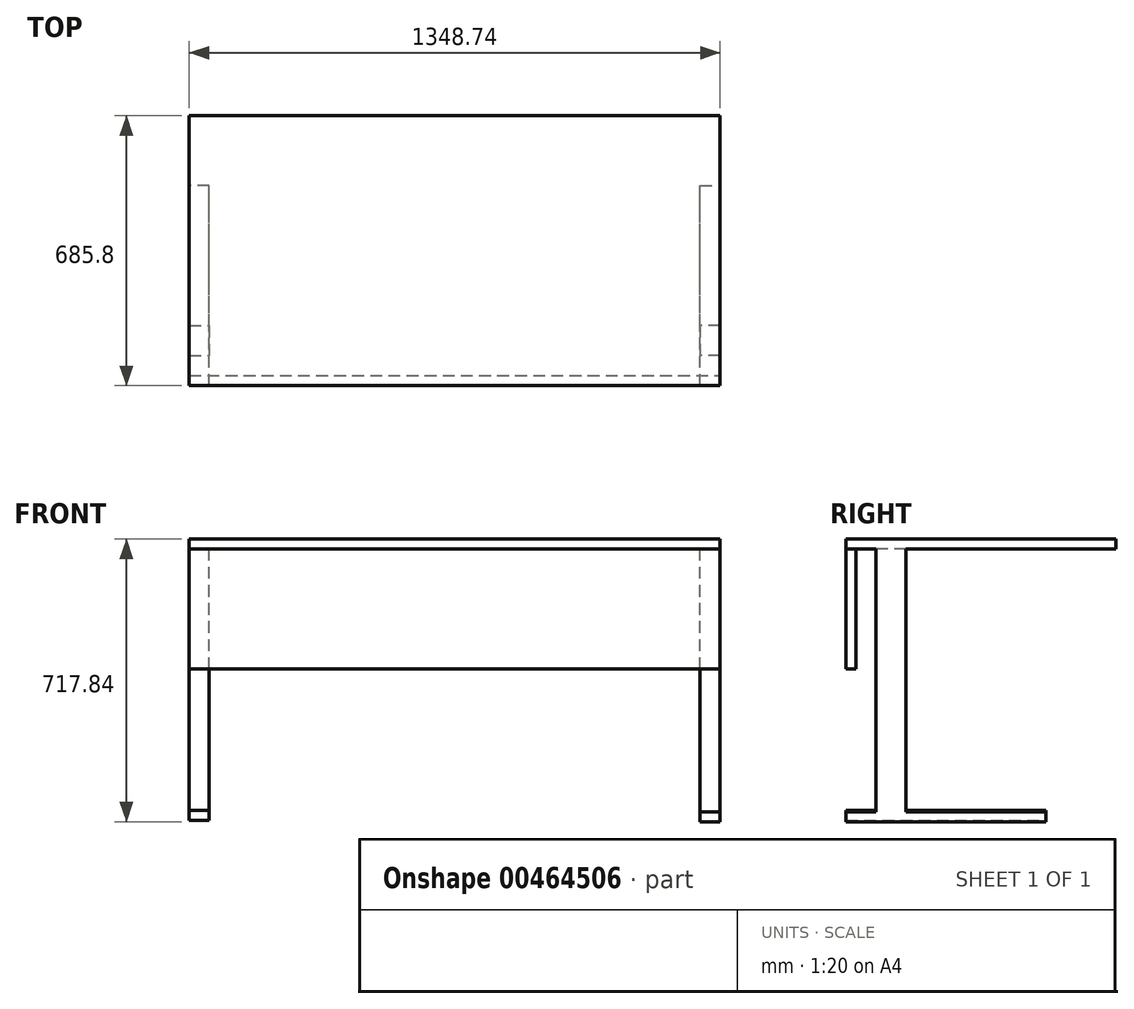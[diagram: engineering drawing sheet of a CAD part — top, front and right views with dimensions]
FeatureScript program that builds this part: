
annotation { "Feature Type Name" : "Feature", "Feature Type Description" : "" }
export const myFeature = defineFeature(function(context is Context, id is Id, definition is map)
    precondition{}
    {
        {
            var Q0;
            Q0=qCreatedBy(makeId("Top.planeOp"),FACE);
            var sketch = newSketch(context, id + "F0", { "sketchPlane" : qUnion([Q0])});
            skLineSegment(sketch, "E0.bottom", {"start": v(-75.15, -75.42) * mm, "end": v(1273.6, -75.42) * mm});
            skLineSegment(sketch, "E0.top", {"start": v(-75.15, 610.38) * mm, "end": v(1273.6, 610.38) * mm});
            skLineSegment(sketch, "E0.left", {"start": v(-75.15, -75.42) * mm, "end": v(-75.15, 610.38) * mm});
            skLineSegment(sketch, "E0.right", {"start": v(1273.6, -75.42) * mm, "end": v(1273.6, 610.38) * mm});
            skLineSegment(sketch, "E1.bottom", {"start": v(-75.15, 610.38) * mm, "end": v(5.86, 610.38) * mm});
            skLineSegment(sketch, "E1.left", {"start": v(-75.15, 610.38) * mm, "end": v(-75.15, 533.58) * mm});
            skSolve(sketch);
        }
        {
            var Q0;
            Q0 = qSketchRegion(id + "F0", true);
            extrude(context, id + "F1", {"entities" : qUnion([Q0]), "depth" : 25.4 * mm});
        }
        {
            var Q0;
            Q0=makeQuery(id+"F1.opExtrude","CAP_FACE",FACE,{"disambiguationData":[OSD([sQuery(id+"F0.wireOp",EDGE,"E0.bottom"),sQuery(id+"F0.wireOp",EDGE,"E0.top"),sQuery(id+"F0.wireOp",EDGE,"E0.left"),sQuery(id+"F0.wireOp",EDGE,"E0.right"),sQuery(id+"F0.wireOp",EDGE,"E1.bottom"),sQuery(id+"F0.wireOp",EDGE,"E1.left")])],"isStart":true});
            var sketch = newSketch(context, id + "F2", { "sketchPlane" : qUnion([Q0])});
            skLineSegment(sketch, "E2.bottom", {"start": v(-75.15, -76.98) * mm, "end": v(-24.35, -76.98) * mm});
            skLineSegment(sketch, "E2.top", {"start": v(-75.15, -0.78) * mm, "end": v(-24.35, -0.78) * mm});
            skLineSegment(sketch, "E2.left", {"start": v(-75.15, -76.98) * mm, "end": v(-75.15, -0.78) * mm});
            skLineSegment(sketch, "E2.right", {"start": v(-24.35, -76.98) * mm, "end": v(-24.35, -0.78) * mm});
            skLineSegment(sketch, "E3.bottom", {"start": v(1273.6, -76.98) * mm, "end": v(1222.8, -76.98) * mm});
            skLineSegment(sketch, "E3.top", {"start": v(1273.6, -0.78) * mm, "end": v(1222.8, -0.78) * mm});
            skLineSegment(sketch, "E3.left", {"start": v(1273.6, -76.98) * mm, "end": v(1273.6, -0.78) * mm});
            skLineSegment(sketch, "E3.right", {"start": v(1222.8, -76.98) * mm, "end": v(1222.8, -0.78) * mm});
            skSolve(sketch);
        }
        {
            var Q0;
            Q0=makeQuery(id+"F2.imprint","IMPRINT",FACE,{"disambiguationData":[TD([[makeQuery(id+"F2.imprint","IMPRINT",EDGE,{"derivedFrom":sQuery(id+"F2.wireOp",EDGE,"E2.bottom")}),1.0]])]});
            var Q1;
            Q1=makeQuery(id+"F2.imprint","IMPRINT",FACE,{"disambiguationData":[TD([[makeQuery(id+"F2.imprint","IMPRINT",EDGE,{"derivedFrom":sQuery(id+"F2.wireOp",EDGE,"E3.bottom")}),-1.0]])]});
            extrude(context, id + "F3", {"entities" : qUnion([Q0, Q1]), "operationType" : NewBodyOperationType.ADD, "depth" : 685.8 * mm});
        }
        {
            var Q0;
            Q0=makeQuery(id+"F3.boolean.opBoolean","MERGE",FACE,{"derivedFrom":[makeQuery(id+"F1.opExtrude","SWEPT_FACE",FACE,{"disambiguationData":[OSD([sQuery(id+"F0.wireOp",EDGE,"E0.right")])]}),makeQuery(id+"F3.opExtrude","SWEPT_FACE",FACE,{"disambiguationData":[OSD([sQuery(id+"F2.wireOp",EDGE,"E3.left")])]})]});
            var sketch = newSketch(context, id + "F4", { "sketchPlane" : qUnion([Q0])});
            skLineSegment(sketch, "E4.bottom", {"start": v(-75.42, -667.04) * mm, "end": v(432.58, -667.04) * mm});
            skLineSegment(sketch, "E4.top", {"start": v(-75.42, -692.44) * mm, "end": v(432.58, -692.44) * mm});
            skLineSegment(sketch, "E4.left", {"start": v(-75.42, -667.04) * mm, "end": v(-75.42, -692.44) * mm});
            skLineSegment(sketch, "E4.right", {"start": v(432.58, -667.04) * mm, "end": v(432.58, -692.44) * mm});
            skSolve(sketch);
        }
        {
            var Q0;
            Q0 = qSketchRegion(id + "FHoVi1I3KBmm1qh_1", true);
            var Q1;
            Q1=makeQuery(id+"F4.imprint","IMPRINT",FACE,{"disambiguationData":[TD([[makeQuery(id+"F4.imprint","IMPRINT",EDGE,{"derivedFrom":sQuery(id+"F4.wireOp",EDGE,"E4.top")}),1.0]])]});
            extrude(context, id + "F5", {"entities" : qUnion([Q0, Q1]), "operationType" : NewBodyOperationType.ADD, "oppositeDirection" : true, "depth" : 50.8 * mm});
        }
        {
            var Q0;
            Q0=makeQuery(id+"F3.boolean.opBoolean","MERGE",FACE,{"derivedFrom":[makeQuery(id+"F1.opExtrude","SWEPT_FACE",FACE,{"disambiguationData":[OSD([sQuery(id+"F0.wireOp",EDGE,"E0.left"),sQuery(id+"F0.wireOp",EDGE,"E1.left")])]}),makeQuery(id+"F3.opExtrude","SWEPT_FACE",FACE,{"disambiguationData":[OSD([sQuery(id+"F2.wireOp",EDGE,"E2.left")])]})]});
            var sketch = newSketch(context, id + "F6", { "sketchPlane" : qUnion([Q0])});
            skPoint(sketch, "E5.firstSnap0", {"position": v(-38.88, -685.8) * mm});
            skLineSegment(sketch, "E6.bottom", {"start": v(75.42, -664.12) * mm, "end": v(-432.58, -664.12) * mm});
            skLineSegment(sketch, "E6.top", {"start": v(75.42, -689.52) * mm, "end": v(-432.58, -689.52) * mm});
            skLineSegment(sketch, "E6.left", {"start": v(75.42, -664.12) * mm, "end": v(75.42, -689.52) * mm});
            skLineSegment(sketch, "E6.right", {"start": v(-432.58, -664.12) * mm, "end": v(-432.58, -689.52) * mm});
            skSolve(sketch);
        }
        {
            var Q0;
            {var subQ1=sQuery(id+"F2.wireOp",EDGE,"E2.left");var subQ8=makeQuery(id+"F3.opExtrude","CAP_EDGE",EDGE,{"disambiguationData":[OSD([subQ1])],"isStart":false});Q0=makeQuery(id+"F6.imprint","IMPRINT",FACE,{"disambiguationData":[TD([[makeQuery(id+"F6.imprint","IMPRINT",EDGE,{"derivedFrom":subQ8}),1.0]])]});}
            var Q1;
            Q1=makeQuery(id+"F6.imprint","IMPRINT",FACE,{"disambiguationData":[TD([[makeQuery(id+"F6.imprint","IMPRINT",EDGE,{"derivedFrom":sQuery(id+"F6.wireOp",EDGE,"E6.top")}),-1.0]])]});
            extrude(context, id + "F7", {"entities" : qUnion([Q0, Q1]), "operationType" : NewBodyOperationType.ADD, "oppositeDirection" : true, "depth" : 50.8 * mm});
        }
        {
            var Q0;
            Q0=makeQuery(id+"F1.opExtrude","SWEPT_FACE",FACE,{"disambiguationData":[OSD([sQuery(id+"F0.wireOp",EDGE,"E0.bottom")])]});
            var sketch = newSketch(context, id + "F8", { "sketchPlane" : qUnion([Q0])});
            skLineSegment(sketch, "E7.bottom", {"start": v(1273.6, 0) * mm, "end": v(-75.15, 0) * mm});
            skLineSegment(sketch, "E7.top", {"start": v(1273.6, -304.8) * mm, "end": v(-75.15, -304.8) * mm});
            skLineSegment(sketch, "E7.left", {"start": v(1273.6, 0) * mm, "end": v(1273.6, -304.8) * mm});
            skLineSegment(sketch, "E7.right", {"start": v(-75.15, 0) * mm, "end": v(-75.15, -304.8) * mm});
            skSolve(sketch);
        }
        {
            var Q0;
            Q0=makeQuery(id+"F8.imprint","IMPRINT",FACE,{"disambiguationData":[TD([[makeQuery(id+"F8.imprint","IMPRINT",EDGE,{"derivedFrom":sQuery(id+"F8.wireOp",EDGE,"E7.bottom")}),-1.0]])]});
            extrude(context, id + "F9", {"entities" : qUnion([Q0]), "oppositeDirection" : true, "depth" : 25.4 * mm});
        }
    });
